FCSTD DOCUMENT  (FreeCAD 1.1R20260325 (Git shallow))
Label: NFC
License: All rights reserved
objects: App::Point×2, Sketcher::SketchObject×1, PartDesign::Body×1, App::Part×1
note: 3 computed .brp shape members not serialized (recipe doc carries the construction recipe); baked Part::Feature solids carry a one-line shape summary decoded from their .brp

FEATURE [App::Point] Origin001
  Role = Origin
FEATURE [App::Point] Origin003
  Role = Origin
FEATURE [Sketcher::SketchObject] Sketch
  ArcFitTolerance = 1e-06
  AttachmentSupport = -> [Origin002]
  ExternalTypes = [0]
  FullyConstrained = false
  MakeInternals = false
  MapMode = 5
  _ExternalGeoVersion = 1
  sketch-geometry (132):
    g0: LineSegment StartX=-24 StartY=-1.7 StartZ=0 EndX=-24 EndY=-13 EndZ=0
    g1: ArcOfCircle CenterX=-23 CenterY=-13 CenterZ=0 NormalX=0 NormalY=0 NormalZ=1 AngleXU=0 Radius=0.999985 StartAngle=3.14159 EndAngle=4.71239
    g2: LineSegment StartX=-24.8 StartY=-1.7 StartZ=0 EndX=-24.8 EndY=-13 EndZ=0
    g3: ArcOfCircle CenterX=-23 CenterY=-13 CenterZ=0 NormalX=0 NormalY=0 NormalZ=1 AngleXU=0 Radius=1.79998 StartAngle=3.14159 EndAngle=4.71239
    g4: LineSegment StartX=-23 StartY=-14 StartZ=0 EndX=23 EndY=-14 EndZ=0
    g5: LineSegment StartX=-23 StartY=-14.8 StartZ=0 EndX=23 EndY=-14.8 EndZ=0
    g6: ArcOfCircle CenterX=23 CenterY=-13 CenterZ=0 NormalX=0 NormalY=0 NormalZ=1 AngleXU=0 Radius=0.999985 StartAngle=4.71239 EndAngle=6.28318
    g7: ArcOfCircle CenterX=23 CenterY=-13 CenterZ=0 NormalX=0 NormalY=0 NormalZ=1 AngleXU=0 Radius=1.79998 StartAngle=4.71239 EndAngle=6.28319
    g8: LineSegment StartX=24 StartY=-13 StartZ=0 EndX=24 EndY=13 EndZ=0
    g9: LineSegment StartX=24.8 StartY=-13 StartZ=0 EndX=24.8 EndY=13 EndZ=0
    g10: ArcOfCircle CenterX=23 CenterY=13 CenterZ=0 NormalX=0 NormalY=0 NormalZ=1 AngleXU=0 Radius=0.999985 StartAngle=-9e-16 EndAngle=1.5708
    g11: ArcOfCircle CenterX=23 CenterY=13 CenterZ=0 NormalX=0 NormalY=0 NormalZ=1 AngleXU=0 Radius=1.79998 StartAngle=1e-16 EndAngle=1.5708
    g12: LineSegment StartX=23 StartY=14 StartZ=0 EndX=-23 EndY=14 EndZ=0
    g13: LineSegment StartX=23 StartY=14.8 StartZ=0 EndX=-23 EndY=14.8 EndZ=0
    g14: ArcOfCircle CenterX=-23 CenterY=13 CenterZ=0 NormalX=0 NormalY=0 NormalZ=1 AngleXU=0 Radius=0.999985 StartAngle=1.5708 EndAngle=3.14159
    g15: ArcOfCircle CenterX=-23 CenterY=13 CenterZ=0 NormalX=0 NormalY=0 NormalZ=1 AngleXU=0 Radius=1.79998 StartAngle=1.5708 EndAngle=3.14159
    g16: LineSegment StartX=-24.8 StartY=-1.7 StartZ=0 EndX=-24 EndY=-1.7 EndZ=0
    g17: LineSegment StartX=-25.3 StartY=-0.770395 StartZ=0 EndX=-25.3 EndY=-13 EndZ=0
    g18: LineSegment StartX=-26.1 StartY=-0.770395 StartZ=0 EndX=-26.1 EndY=-13 EndZ=0
    g19: ArcOfCircle CenterX=-23 CenterY=-13 CenterZ=0 NormalX=0 NormalY=0 NormalZ=1 AngleXU=0 Radius=2.29998 StartAngle=3.14159 EndAngle=4.71239
    g20: ArcOfCircle CenterX=-23 CenterY=-13 CenterZ=0 NormalX=0 NormalY=0 NormalZ=1 AngleXU=0 Radius=3.09998 StartAngle=3.14159 EndAngle=4.71239
    g21: LineSegment StartX=-23 StartY=-15.3 StartZ=0 EndX=23 EndY=-15.3 EndZ=0
    g22: LineSegment StartX=-23 StartY=-16.1 StartZ=0 EndX=23 EndY=-16.1 EndZ=0
    g23: ArcOfCircle CenterX=23 CenterY=-13 CenterZ=0 NormalX=0 NormalY=0 NormalZ=1 AngleXU=0 Radius=2.29998 StartAngle=4.71239 EndAngle=6.28318
    g24: ArcOfCircle CenterX=23 CenterY=-13 CenterZ=0 NormalX=0 NormalY=0 NormalZ=1 AngleXU=0 Radius=3.09998 StartAngle=4.71239 EndAngle=6.28318
    g25: LineSegment StartX=25.3 StartY=-13 StartZ=0 EndX=25.3 EndY=13 EndZ=0
    g26: LineSegment StartX=26.1 StartY=-13 StartZ=0 EndX=26.1 EndY=13 EndZ=0
    g27: ArcOfCircle CenterX=23 CenterY=13 CenterZ=0 NormalX=0 NormalY=0 NormalZ=1 AngleXU=0 Radius=2.29998 StartAngle=2e-16 EndAngle=1.5708
    g28: ArcOfCircle CenterX=23 CenterY=13 CenterZ=0 NormalX=0 NormalY=0 NormalZ=1 AngleXU=0 Radius=3.09998 StartAngle=2e-16 EndAngle=1.5708
    g29: LineSegment StartX=23 StartY=15.3 StartZ=0 EndX=-23 EndY=15.3 EndZ=0
    g30: LineSegment StartX=23 StartY=16.1 StartZ=0 EndX=-23 EndY=16.1 EndZ=0
    g31: ArcOfCircle CenterX=-23 CenterY=13 CenterZ=0 NormalX=0 NormalY=0 NormalZ=1 AngleXU=0 Radius=2.29998 StartAngle=1.5708 EndAngle=3.14159
    g32: ArcOfCircle CenterX=-23 CenterY=13 CenterZ=0 NormalX=0 NormalY=0 NormalZ=1 AngleXU=0 Radius=3.09998 StartAngle=1.5708 EndAngle=3.14159
    g33: LineSegment StartX=-26.6 StartY=-0.770395 StartZ=0 EndX=-26.6 EndY=-13 EndZ=0
    g34: LineSegment StartX=-27.4 StartY=-0.770395 StartZ=0 EndX=-27.4 EndY=-13 EndZ=0
    g35: ArcOfCircle CenterX=-23 CenterY=-13 CenterZ=0 NormalX=0 NormalY=0 NormalZ=1 AngleXU=0 Radius=3.59998 StartAngle=3.14159 EndAngle=4.71239
    g36: ArcOfCircle CenterX=-23 CenterY=-13 CenterZ=0 NormalX=0 NormalY=0 NormalZ=1 AngleXU=0 Radius=4.39998 StartAngle=3.14159 EndAngle=4.71239
    g37: LineSegment StartX=-23 StartY=-16.6 StartZ=0 EndX=23 EndY=-16.6 EndZ=0
    g38: LineSegment StartX=-23 StartY=-17.4 StartZ=0 EndX=23 EndY=-17.4 EndZ=0
    g39: ArcOfCircle CenterX=23 CenterY=-13 CenterZ=0 NormalX=0 NormalY=0 NormalZ=1 AngleXU=0 Radius=3.59998 StartAngle=4.71239 EndAngle=6.28318
    g40: ArcOfCircle CenterX=23 CenterY=-13 CenterZ=0 NormalX=0 NormalY=0 NormalZ=1 AngleXU=0 Radius=4.39998 StartAngle=4.71239 EndAngle=6.28318
    g41: LineSegment StartX=26.6 StartY=-13 StartZ=0 EndX=26.6 EndY=13 EndZ=0
    g42: LineSegment StartX=27.4 StartY=-13 StartZ=0 EndX=27.4 EndY=13 EndZ=0
    g43: ArcOfCircle CenterX=23 CenterY=13 CenterZ=0 NormalX=0 NormalY=0 NormalZ=1 AngleXU=0 Radius=3.59998 StartAngle=2e-16 EndAngle=1.5708
    g44: ArcOfCircle CenterX=23 CenterY=13 CenterZ=0 NormalX=0 NormalY=0 NormalZ=1 AngleXU=0 Radius=4.39998 StartAngle=0 EndAngle=1.5708
    g45: LineSegment StartX=23 StartY=16.6 StartZ=0 EndX=-23 EndY=16.6 EndZ=0
    g46: LineSegment StartX=23 StartY=17.4 StartZ=0 EndX=-23 EndY=17.4 EndZ=0
    g47: ArcOfCircle CenterX=-23 CenterY=13 CenterZ=0 NormalX=0 NormalY=0 NormalZ=1 AngleXU=0 Radius=3.59998 StartAngle=1.5708 EndAngle=3.14159
    g48: ArcOfCircle CenterX=-23 CenterY=13 CenterZ=0 NormalX=0 NormalY=0 NormalZ=1 AngleXU=0 Radius=4.39998 StartAngle=1.5708 EndAngle=3.14159
    g49: LineSegment StartX=-27.9 StartY=-0.770395 StartZ=0 EndX=-27.9 EndY=-13 EndZ=0
    g50: LineSegment StartX=-28.7 StartY=-0.770395 StartZ=0 EndX=-28.7 EndY=-13 EndZ=0
    g51: ArcOfCircle CenterX=-23 CenterY=-13 CenterZ=0 NormalX=0 NormalY=0 NormalZ=1 AngleXU=0 Radius=4.89998 StartAngle=3.14159 EndAngle=4.71239
    g52: ArcOfCircle CenterX=-23 CenterY=-13 CenterZ=0 NormalX=0 NormalY=0 NormalZ=1 AngleXU=0 Radius=5.69998 StartAngle=3.14159 EndAngle=4.71239
    g53: LineSegment StartX=-23 StartY=-17.9 StartZ=0 EndX=23 EndY=-17.9 EndZ=0
    g54: LineSegment StartX=-23 StartY=-18.7 StartZ=0 EndX=23 EndY=-18.7 EndZ=0
    g55: ArcOfCircle CenterX=23 CenterY=-13 CenterZ=0 NormalX=0 NormalY=0 NormalZ=1 AngleXU=0 Radius=4.89998 StartAngle=4.71239 EndAngle=6.28318
    g56: ArcOfCircle CenterX=23 CenterY=-13 CenterZ=0 NormalX=0 NormalY=0 NormalZ=1 AngleXU=0 Radius=5.69998 StartAngle=4.71239 EndAngle=6.28318
    g57: LineSegment StartX=27.9 StartY=-13 StartZ=0 EndX=27.9 EndY=13 EndZ=0
    g58: LineSegment StartX=28.7 StartY=-13 StartZ=0 EndX=28.7 EndY=13 EndZ=0
    g59: ArcOfCircle CenterX=23 CenterY=13 CenterZ=0 NormalX=0 NormalY=0 NormalZ=1 AngleXU=0 Radius=4.89998 StartAngle=8.7e-15 EndAngle=1.5708
    g60: ArcOfCircle CenterX=23 CenterY=13 CenterZ=0 NormalX=0 NormalY=0 NormalZ=1 AngleXU=0 Radius=5.69999 StartAngle=6.28318 EndAngle=7.85398
    g61: LineSegment StartX=23 StartY=17.9 StartZ=0 EndX=-23 EndY=17.9 EndZ=0
    g62: LineSegment StartX=23 StartY=18.7 StartZ=0 EndX=-23 EndY=18.7 EndZ=0
    g63: ArcOfCircle CenterX=-23 CenterY=13 CenterZ=0 NormalX=0 NormalY=0 NormalZ=1 AngleXU=0 Radius=4.9 StartAngle=1.5708 EndAngle=3.14159
    g64: ArcOfCircle CenterX=-23 CenterY=13 CenterZ=0 NormalX=0 NormalY=0 NormalZ=1 AngleXU=0 Radius=5.70002 StartAngle=1.5708 EndAngle=3.14159
    g65: LineSegment StartX=-29.2 StartY=-0.770387 StartZ=0 EndX=-29.2 EndY=-13 EndZ=0
    g66: LineSegment StartX=-30 StartY=-0.770374 StartZ=0 EndX=-30 EndY=-13 EndZ=0
    g67: ArcOfCircle CenterX=-23 CenterY=-13 CenterZ=0 NormalX=0 NormalY=0 NormalZ=1 AngleXU=0 Radius=6.19998 StartAngle=3.14159 EndAngle=4.71239
    g68: ArcOfCircle CenterX=-23 CenterY=-13 CenterZ=0 NormalX=0 NormalY=0 NormalZ=1 AngleXU=0 Radius=6.99998 StartAngle=3.14159 EndAngle=4.71239
    g69: LineSegment StartX=-23 StartY=-19.2 StartZ=0 EndX=23 EndY=-19.2 EndZ=0
    g70: LineSegment StartX=-23 StartY=-20 StartZ=0 EndX=23 EndY=-20 EndZ=0
    g71: ArcOfCircle CenterX=23 CenterY=-13 CenterZ=0 NormalX=0 NormalY=0 NormalZ=1 AngleXU=0 Radius=6.2 StartAngle=4.71239 EndAngle=6.28318
    g72: ArcOfCircle CenterX=23 CenterY=-13 CenterZ=0 NormalX=0 NormalY=0 NormalZ=1 AngleXU=0 Radius=7 StartAngle=4.71239 EndAngle=6.28319
    g73: LineSegment StartX=29.2 StartY=-13 StartZ=0 EndX=29.2 EndY=13 EndZ=0
    g74: LineSegment StartX=30 StartY=-13 StartZ=0 EndX=30 EndY=13 EndZ=0
    g75: ArcOfCircle CenterX=23 CenterY=13 CenterZ=0 NormalX=0 NormalY=0 NormalZ=1 AngleXU=0 Radius=6.20002 StartAngle=6.28318 EndAngle=7.85398
    g76: ArcOfCircle CenterX=23 CenterY=13 CenterZ=0 NormalX=0 NormalY=0 NormalZ=1 AngleXU=0 Radius=7 StartAngle=0 EndAngle=1.5708
    g77: LineSegment StartX=23 StartY=19.2 StartZ=0 EndX=-23 EndY=19.2 EndZ=0
    g78: LineSegment StartX=23 StartY=20 StartZ=0 EndX=-23 EndY=20 EndZ=0
    g79: ArcOfCircle CenterX=-23 CenterY=13 CenterZ=0 NormalX=0 NormalY=0 NormalZ=1 AngleXU=0 Radius=6.20002 StartAngle=1.5708 EndAngle=3.14159
    g80: ArcOfCircle CenterX=-23 CenterY=13 CenterZ=0 NormalX=0 NormalY=0 NormalZ=1 AngleXU=0 Radius=7.00002 StartAngle=1.5708 EndAngle=3.14159
    g81: LineSegment StartX=-24 StartY=13 StartZ=0 EndX=-24 EndY=4.7704 EndZ=0
    g82: LineSegment StartX=-24.8 StartY=13 StartZ=0 EndX=-24.8 EndY=4.7704 EndZ=0
    g83: LineSegment StartX=-24.2381 StartY=3.26733 StartZ=0 EndX=-25.0619 EndY=0.732672 EndZ=0
    g84: LineSegment StartX=-25.0381 StartY=3.26733 StartZ=0 EndX=-25.8619 EndY=0.732672 EndZ=0
    g85: LineSegment StartX=-25.3 StartY=13 StartZ=0 EndX=-25.3 EndY=4.7704 EndZ=0
    g86: LineSegment StartX=-26.1 StartY=13 StartZ=0 EndX=-26.1 EndY=4.7704 EndZ=0
    g87: LineSegment StartX=-26.6 StartY=13 StartZ=0 EndX=-26.6 EndY=4.7704 EndZ=0
    g88: LineSegment StartX=-27.4 StartY=13 StartZ=0 EndX=-27.4 EndY=4.7704 EndZ=0
    g89: LineSegment StartX=-27.9 StartY=13 StartZ=0 EndX=-27.9 EndY=4.77039 EndZ=0
    g90: LineSegment StartX=-28.7 StartY=13 StartZ=0 EndX=-28.7 EndY=4.77037 EndZ=0
    g91: LineSegment StartX=-29.2 StartY=13 StartZ=0 EndX=-29.2 EndY=5.7 EndZ=0
    g92: LineSegment StartX=-25.5381 StartY=3.26733 StartZ=0 EndX=-26.3619 EndY=0.732672 EndZ=0
    g93: LineSegment StartX=-26.3381 StartY=3.26733 StartZ=0 EndX=-27.1619 EndY=0.732672 EndZ=0
    g94: LineSegment StartX=-26.8381 StartY=3.26733 StartZ=0 EndX=-27.6619 EndY=0.732672 EndZ=0
    g95: LineSegment StartX=-27.6381 StartY=3.26733 StartZ=0 EndX=-28.4619 EndY=0.732672 EndZ=0
    g96: LineSegment StartX=-28.1381 StartY=3.26734 StartZ=0 EndX=-28.9619 EndY=0.732665 EndZ=0
    g97: LineSegment StartX=-28.9381 StartY=3.26735 StartZ=0 EndX=-29.7619 EndY=0.732654 EndZ=0
    g98: LineSegment StartX=-30 StartY=13 StartZ=0 EndX=-30 EndY=5.7 EndZ=0
    g99: LineSegment StartX=-29.2 StartY=5.7 StartZ=0 EndX=-30 EndY=5.7 EndZ=0
    g100: ArcOfCircle CenterX=-32.7629 CenterY=4.77039 CenterZ=0 NormalX=0 NormalY=0 NormalZ=1 AngleXU=0 Radius=4.86294 StartAngle=5.96896 EndAngle=6.28319
    g101: GeomPoint [constr] X=-27.9 Y=4 Z=0
    g102: ArcOfCircle CenterX=-32.2629 CenterY=4.7704 CenterZ=0 NormalX=0 NormalY=0 NormalZ=1 AngleXU=0 Radius=4.86294 StartAngle=5.96895 EndAngle=6.28319
    g103: GeomPoint [constr] X=-27.4 Y=4 Z=0
    g104: ArcOfCircle CenterX=-31.4629 CenterY=4.7704 CenterZ=0 NormalX=0 NormalY=0 NormalZ=1 AngleXU=0 Radius=4.86294 StartAngle=5.96895 EndAngle=6.28319
    g105: GeomPoint [constr] X=-26.6 Y=4 Z=0
    g106: ArcOfCircle CenterX=-30.9629 CenterY=4.7704 CenterZ=0 NormalX=0 NormalY=0 NormalZ=1 AngleXU=0 Radius=4.86294 StartAngle=5.96895 EndAngle=6.28319
    g107: GeomPoint [constr] X=-26.1 Y=4 Z=0
    g108: ArcOfCircle CenterX=-30.1629 CenterY=4.7704 CenterZ=0 NormalX=0 NormalY=0 NormalZ=1 AngleXU=0 Radius=4.86294 StartAngle=5.96895 EndAngle=6.28319
    g109: GeomPoint [constr] X=-25.3 Y=4 Z=0
    g110: ArcOfCircle CenterX=-29.6629 CenterY=4.7704 CenterZ=0 NormalX=0 NormalY=0 NormalZ=1 AngleXU=0 Radius=4.86294 StartAngle=5.96895 EndAngle=6.28319
    g111: GeomPoint [constr] X=-24.8 Y=4 Z=0
    g112: ArcOfCircle CenterX=-28.8629 CenterY=4.7704 CenterZ=0 NormalX=0 NormalY=0 NormalZ=1 AngleXU=0 Radius=4.86294 StartAngle=5.96895 EndAngle=6.28319
    g113: GeomPoint [constr] X=-24 Y=4 Z=0
    g114: ArcOfCircle CenterX=-33.563 CenterY=4.77037 CenterZ=0 NormalX=0 NormalY=0 NormalZ=1 AngleXU=0 Radius=4.86294 StartAngle=5.96896 EndAngle=6.28319
    g115: GeomPoint [constr] X=-28.7 Y=4 Z=0
    g116: ArcOfCircle CenterX=-25.137 CenterY=-0.770374 CenterZ=0 NormalX=0 NormalY=0 NormalZ=1 AngleXU=0 Radius=4.86294 StartAngle=2.82737 EndAngle=3.14159
    g117: GeomPoint [constr] X=-30 Y=1.6e-15 Z=0
    g118: ArcOfCircle CenterX=-24.337 CenterY=-0.770387 CenterZ=0 NormalX=0 NormalY=0 NormalZ=1 AngleXU=0 Radius=4.86294 StartAngle=2.82736 EndAngle=3.14159
    g119: GeomPoint [constr] X=-29.2 Y=3.3e-15 Z=0
    g120: ArcOfCircle CenterX=-23.837 CenterY=-0.770395 CenterZ=0 NormalX=0 NormalY=0 NormalZ=1 AngleXU=0 Radius=4.86294 StartAngle=2.82736 EndAngle=3.14159
    g121: GeomPoint [constr] X=-28.7 Y=-1.6e-15 Z=0
    g122: ArcOfCircle CenterX=-23.037 CenterY=-0.770395 CenterZ=0 NormalX=0 NormalY=0 NormalZ=1 AngleXU=0 Radius=4.86294 StartAngle=2.82736 EndAngle=3.14159
    g123: GeomPoint [constr] X=-27.9 Y=-1.6e-15 Z=0
    g124: ArcOfCircle CenterX=-22.537 CenterY=-0.770395 CenterZ=0 NormalX=0 NormalY=0 NormalZ=1 AngleXU=0 Radius=4.86294 StartAngle=2.82736 EndAngle=3.14159
    g125: GeomPoint [constr] X=-27.4 Y=1.6e-15 Z=0
    g126: ArcOfCircle CenterX=-21.737 CenterY=-0.770395 CenterZ=0 NormalX=0 NormalY=0 NormalZ=1 AngleXU=0 Radius=4.86294 StartAngle=2.82736 EndAngle=3.14159
    g127: GeomPoint [constr] X=-26.6 Y=-1.6e-15 Z=0
    g128: ArcOfCircle CenterX=-21.237 CenterY=-0.770395 CenterZ=0 NormalX=0 NormalY=0 NormalZ=1 AngleXU=0 Radius=4.86294 StartAngle=2.82736 EndAngle=3.14159
    g129: GeomPoint [constr] X=-26.1 Y=0 Z=0
    g130: ArcOfCircle CenterX=-20.437 CenterY=-0.770395 CenterZ=0 NormalX=0 NormalY=0 NormalZ=1 AngleXU=0 Radius=4.86294 StartAngle=2.82736 EndAngle=3.14159
    g131: GeomPoint [constr] X=-25.3 Y=-1.6e-15 Z=0
  constraints (317):
    c: Vertical(g0)
    c: Angle(g1) = 1.5708
    c: Vertical(g2)
    c: Angle(g3) = 1.5708
    c: Coincident(g3,g1)
    c: Coincident(g3,g2)
    c: Horizontal(g1,g2)
    c: DistanceX(g2,g0) = 0.8
    c: Coincident(g4,g1)
    c: Horizontal(g4)
    c: Coincident(g5,g3)
    c: Horizontal(g5)
    c: Angle(g6) = 1.5708
    c: Coincident(g7,g6)
    c: Horizontal(g6,g7)
    c: Coincident(g8,g6)
    c: Vertical(g8)
    c: Coincident(g9,g7)
    c: Vertical(g9)
    c: Horizontal(g8,g9)
    c: Angle(g10) = 1.5708
    c: Coincident(g11,g10)
    c: Coincident(g11,g9)
    c: Vertical(g10,g11)
    c: Coincident(g12,g10)
    c: Horizontal(g12)
    c: Coincident(g13,g11)
    c: Horizontal(g13)
    c: Vertical(g12,g13)
    c: Angle(g14) = 1.5708
    c: Angle(g15) = 1.5708
    c: Coincident(g15,g14)
    c: Coincident(g15,g13)
    c: Tangent(g14,g12) = -1.5708
    c: Tangent(g1,g0) = -1.5708
    c: Tangent(g6,g4) = -1.5708
    c: Tangent(g10,g8) = -1.5708
    c: Coincident(g16,g2)
    c: Coincident(g16,g0)
    c: PointOnObject(g131,g-1)
    c: DistanceX(g131,g2) = 0.5
    c: PointOnObject(g129,g-1)
    c: DistanceX(g129,g131) = 0.8
    c: Vertical(g17)
    c: Vertical(g18)
    c: Horizontal(g17,g18)
    c: Angle(g19) = 1.5708
    c: Coincident(g19,g1)
    c: Angle(g20) = 1.5708
    c: Coincident(g20,g1)
    c: Coincident(g20,g18)
    c: Tangent(g19,g17) = -1.5708
    c: Coincident(g21,g19)
    c: Horizontal(g21)
    c: Tangent(g7,g5) = -1.5708
    c: Coincident(g22,g20)
    c: Horizontal(g22)
    c: Coincident(g23,g6)
    c: Angle(g24) = 1.5708
    c: Coincident(g24,g6)
    c: Tangent(g23,g21) = -1.5708
    c: Tangent(g24,g22) = -1.5708
    c: Horizontal(g23,g24)
    c: Coincident(g25,g23)
    c: Vertical(g25)
    c: Coincident(g26,g24)
    c: Vertical(g26)
    c: Coincident(g27,g10)
    c: Coincident(g28,g10)
    c: Tangent(g28,g26) = -1.5708
    c: Tangent(g27,g25) = -1.5708
    c: Horizontal(g29)
    c: Horizontal(g30)
    c: Angle(g31) = 1.5708
    c: Coincident(g31,g14)
    c: Angle(g32) = 1.5708
    c: Coincident(g32,g14)
    c: Tangent(g32,g30) = -1.5708
    c: Tangent(g31,g29) = -1.5708
    c: PointOnObject(g127,g-1)
    c: PointOnObject(g125,g-1)
    c: DistanceX(g127,g129) = 0.5
    c: DistanceX(g125,g127) = 0.8
    c: Vertical(g33)
    c: Vertical(g34)
    c: Angle(g35) = 1.5708
    c: Coincident(g35,g1)
    c: Angle(g36) = 1.5708
    c: Coincident(g36,g1)
    c: Tangent(g35,g33) = -1.5708
    c: Tangent(g36,g34) = -1.5708
    c: Coincident(g37,g35)
    c: Horizontal(g37)
    c: Coincident(g38,g36)
    c: Horizontal(g38)
    c: Angle(g39) = 1.5708
    c: Coincident(g39,g6)
    c: Angle(g40) = 1.5708
    c: Coincident(g40,g6)
    c: Tangent(g39,g37) = -1.5708
    c: Tangent(g40,g38) = -1.5708
    c: Coincident(g41,g39)
    c: Vertical(g41)
    c: Coincident(g42,g40)
    c: Vertical(g42)
    c: Coincident(g43,g10)
    c: Coincident(g44,g10)
    c: Tangent(g44,g42) = -1.5708
    c: Tangent(g43,g41) = -1.5708
    c: Horizontal(g45)
    c: Horizontal(g46)
    c: Tangent(g46,g44) = -1.5708
    c: Tangent(g45,g43) = -1.5708
    c: Angle(g47) = 1.5708
    c: Coincident(g47,g14)
    c: Angle(g48) = 1.5708
    c: Coincident(g48,g14)
    c: Tangent(g48,g46) = -1.5708
    c: Tangent(g47,g45) = -1.5708
    c: PointOnObject(g123,g-1)
    c: PointOnObject(g121,g-1)
    c: DistanceX(g123,g125) = 0.5
    c: DistanceX(g121,g123) = 0.8
    c: Vertical(g49)
    c: Vertical(g50)
    c: Angle(g51) = 1.5708
    c: Coincident(g51,g1)
    c: Coincident(g51,g49)
    c: Angle(g52) = 1.5708
    c: Coincident(g52,g1)
    c: Coincident(g52,g50)
    c: Horizontal(g53)
    c: Horizontal(g54)
    c: Tangent(g53,g51) = -1.5708
    c: Tangent(g54,g52) = -1.5708
    c: Angle(g55) = 1.5708
    c: Coincident(g55,g6)
    c: Angle(g56) = 1.5708
    c: Coincident(g56,g6)
    c: Tangent(g55,g53) = -1.5708
    c: Tangent(g56,g54) = -1.5708
    c: Coincident(g57,g55)
    c: Vertical(g57)
    c: Tangent(g58,g56) = -1.5708
    c: Angle(g59) = 1.5708
    c: Coincident(g59,g10)
    c: Angle(g60) = 1.5708
    c: Coincident(g60,g10)
    c: Tangent(g60,g58) = -1.5708
    c: Tangent(g59,g57) = -1.5708
    c: Tangent(g62,g60) = -1.5708
    c: Tangent(g61,g59) = -1.5708
    c: Angle(g63) = 1.5708
    c: Coincident(g63,g14)
    c: Angle(g64) = 1.5708
    c: Coincident(g64,g14)
    c: Tangent(g64,g62) = -1.5708
    c: Tangent(g63,g61) = -1.5708
    c: PointOnObject(g119,g-1)
    c: PointOnObject(g117,g-1)
    c: DistanceX(g119,g121) = 0.5
    c: DistanceX(g117,g119) = 0.8
    c: Vertical(g65)
    c: Vertical(g66)
    c: Angle(g67) = 1.5708
    c: Coincident(g67,g1)
    c: Angle(g68) = 1.5708
    c: Coincident(g68,g1)
    c: Tangent(g67,g65) = -1.5708
    c: Tangent(g68,g66) = -1.5708
    c: Tangent(g70,g68) = -1.5708
    c: Tangent(g69,g67) = -1.5708
    c: Angle(g71) = 1.5708
    c: Coincident(g71,g6)
    c: Coincident(g72,g6)
    c: Tangent(g71,g69) = -1.5708
    c: Tangent(g72,g70) = -1.5708
    c: Vertical(g74)
    c: Tangent(g74,g72) = -1.5708
    c: Tangent(g73,g71) = -1.5708
    c: Angle(g75) = 1.5708
    c: Coincident(g75,g10)
    c: Angle(g76) = 1.5708
    c: Coincident(g76,g10)
    c: Tangent(g75,g73) = -1.5708
    c: Tangent(g76,g74) = -1.5708
    c: Coincident(g77,g75)
    c: Horizontal(g77)
    c: Tangent(g78,g76) = -1.5708
    c: Angle(g79) = 1.5708
    c: Coincident(g79,g14)
    c: Angle(g80) = 1.5708
    c: Coincident(g80,g14)
    c: Tangent(g79,g77) = -1.5708
    c: Tangent(g80,g78) = -1.5708
    c: DistanceY(g70,g76) = 40
    c: DistanceX(g80,g74) = 60
    c: Tangent(g30,g28) = -1.5708
    c: Tangent(g29,g27) = -1.5708
    c: Symmetric(g6,g10,g-1)
    c: Symmetric(g1,g14,g-1)
    c: DistanceX(g80,g-1) = 30
    c: Horizontal(g14,g10)
    c: DistanceY(g-1,g14) = 13
    c: Coincident(g81,g14)
    c: Vertical(g81)
    c: Coincident(g82,g15)
    c: Vertical(g82)
    c: Coincident(g85,g31)
    c: Vertical(g85)
    c: Coincident(g86,g32)
    c: Vertical(g86)
    c: Coincident(g87,g47)
    c: Vertical(g87)
    c: Coincident(g88,g48)
    c: Vertical(g88)
    c: Coincident(g89,g63)
    c: Vertical(g89)
    c: Coincident(g90,g64)
    c: Vertical(g90)
    c: Coincident(g91,g79)
    c: Vertical(g91)
    c: Horizontal(g115,g101)
    c: Horizontal(g101,g103)
    c: Horizontal(g103,g105)
    c: Horizontal(g105,g107)
    c: Horizontal(g107,g109)
    c: Horizontal(g109,g111)
    c: Horizontal(g111,g113)
    c: DistanceY(g-1,g113) = 4
    c: DistanceY(g-1,g91) = 5.7
    c: Coincident(g98,g80)
    c: Vertical(g98)
    c: Coincident(g99,g91)
    c: Coincident(g99,g98)
    c: Horizontal(g99)
    c: PointOnObject(g101,g89)
    c: PointOnObject(g101,g96)
    c: Tangent(g89,g100) = 1.5708
    c: Tangent(g96,g100) = 1.5708
    c: PointOnObject(g103,g88)
    c: PointOnObject(g103,g95)
    c: Tangent(g88,g102) = 1.5708
    c: Tangent(g95,g102) = 1.5708
    c: PointOnObject(g105,g87)
    c: PointOnObject(g105,g94)
    c: Tangent(g87,g104) = 1.5708
    c: Tangent(g94,g104) = 1.5708
    c: PointOnObject(g107,g86)
    c: PointOnObject(g107,g93)
    c: Tangent(g86,g106) = 1.5708
    c: Tangent(g93,g106) = 1.5708
    c: PointOnObject(g109,g85)
    c: PointOnObject(g109,g92)
    c: Tangent(g85,g108) = 1.5708
    c: Tangent(g92,g108) = 1.5708
    c: PointOnObject(g111,g82)
    c: PointOnObject(g111,g84)
    c: Tangent(g82,g110) = 1.5708
    c: Tangent(g84,g110) = 1.5708
    c: PointOnObject(g113,g81)
    c: PointOnObject(g113,g83)
    c: Tangent(g81,g112) = 1.5708
    c: Tangent(g83,g112) = 1.5708
    c: PointOnObject(g115,g90)
    c: PointOnObject(g115,g97)
    c: Tangent(g90,g114) = 1.5708
    c: Tangent(g97,g114) = 1.5708
    c: Equal(g114,g100)
    c: Equal(g100,g102)
    c: Equal(g102,g104)
    c: Equal(g104,g106)
    c: Equal(g106,g108)
    c: Equal(g108,g110)
    c: Equal(g110,g112)
    c: PointOnObject(g117,g97)
    c: PointOnObject(g117,g66)
    c: Tangent(g97,g116) = -1.5708
    c: Tangent(g66,g116) = -1.5708
    c: PointOnObject(g119,g96)
    c: PointOnObject(g119,g65)
    c: Tangent(g96,g118) = -1.5708
    c: Tangent(g65,g118) = -1.5708
    c: PointOnObject(g121,g95)
    c: PointOnObject(g121,g50)
    c: Tangent(g95,g120) = -1.5708
    c: Tangent(g50,g120) = -1.5708
    c: PointOnObject(g123,g94)
    c: PointOnObject(g123,g49)
    c: Tangent(g94,g122) = -1.5708
    c: Tangent(g49,g122) = -1.5708
    c: PointOnObject(g125,g93)
    c: PointOnObject(g125,g34)
    c: Tangent(g93,g124) = -1.5708
    c: Tangent(g34,g124) = -1.5708
    c: PointOnObject(g127,g92)
    c: PointOnObject(g127,g33)
    c: Tangent(g92,g126) = -1.5708
    c: Tangent(g33,g126) = -1.5708
    c: PointOnObject(g129,g84)
    c: PointOnObject(g129,g18)
    c: Tangent(g84,g128) = -1.5708
    c: Tangent(g18,g128) = -1.5708
    c: PointOnObject(g131,g83)
    c: PointOnObject(g131,g17)
    c: Tangent(g83,g130) = -1.5708
    c: Tangent(g17,g130) = -1.5708
    c: Equal(g114,g116)
    c: Equal(g116,g118)
    c: Equal(g118,g120)
    c: Equal(g120,g122)
    c: Equal(g122,g124)
    c: Equal(g124,g126)
    c: Equal(g126,g128)
    c: Equal(g128,g130)
    c: Horizontal(g16)
    c: DistanceY(g0,g-1) = 1.7
FEATURE [PartDesign::Body] Body
  AllowCompound = true
  Group = -> [Sketch]
  Origin = -> Origin002
FEATURE [App::Part] Part
  Group = -> [Body]
  Origin = -> Origin
